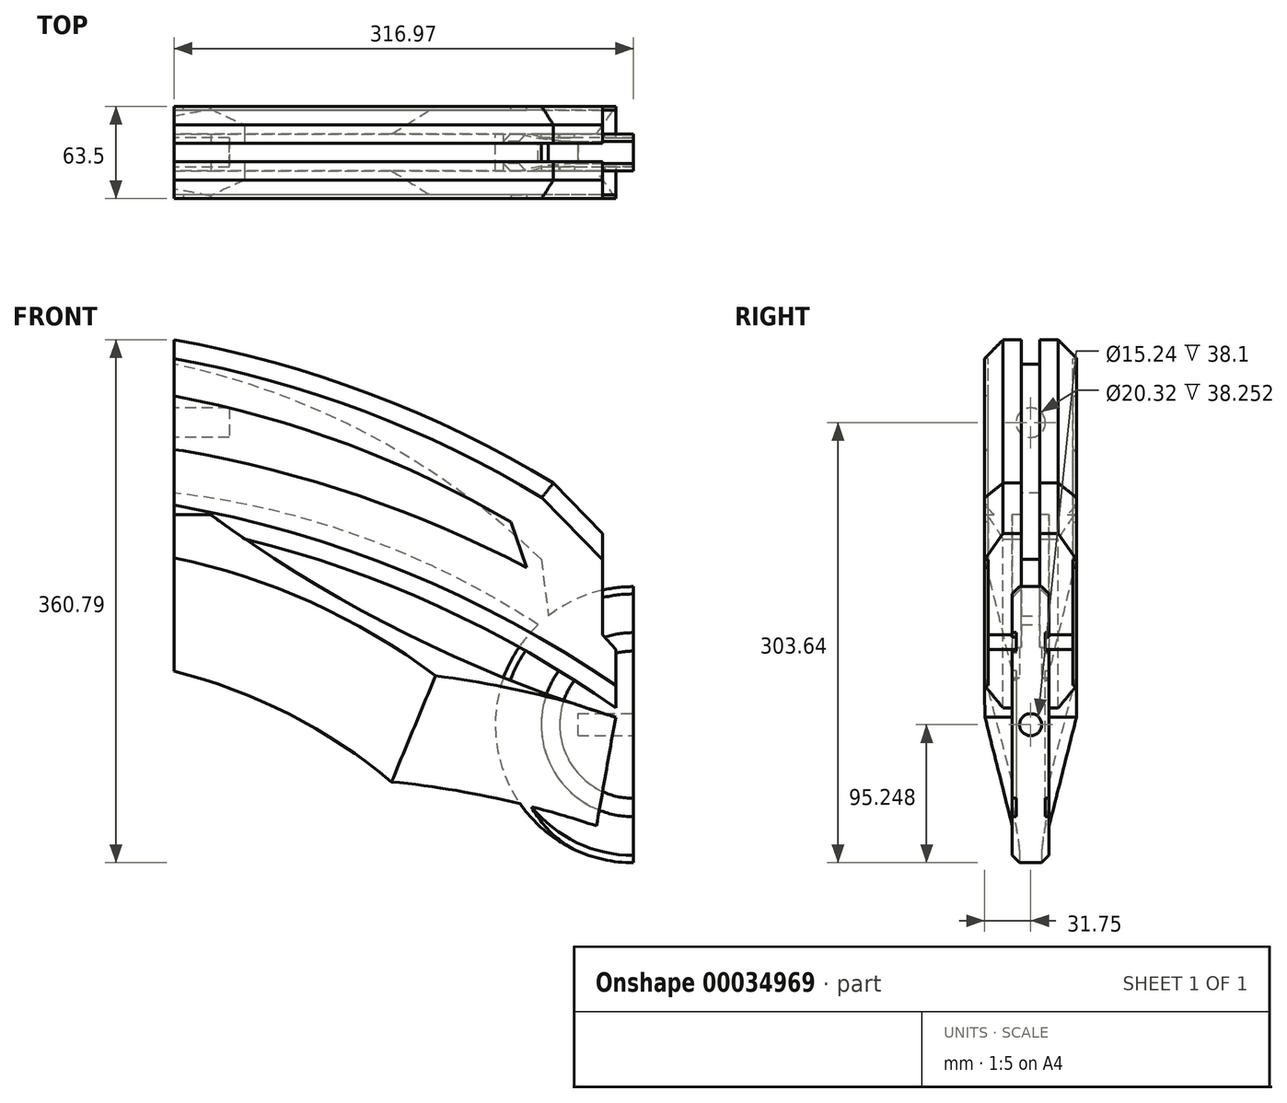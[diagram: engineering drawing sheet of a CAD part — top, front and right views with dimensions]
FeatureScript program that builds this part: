
annotation { "Feature Type Name" : "Feature", "Feature Type Description" : "" }
export const myFeature = defineFeature(function(context is Context, id is Id, definition is map)
    precondition{}
    {
        {
            var Q0;
            Q0=qCreatedBy(makeId("Right.planeOp"),FACE);
            var sketch = newSketch(context, id + "F0", { "sketchPlane" : qUnion([Q0])});
            skCircle(sketch, "E0", {"center": v(0, 0) * mm, "radius": 9.53 * mm});
            skSolve(sketch);
        }
        {
            var Q0;
            Q0=makeQuery(id+"F0.imprint","IMPRINT",FACE,{"disambiguationData":[TD([[makeQuery(id+"F0.imprint","IMPRINT",EDGE,{"derivedFrom":sQuery(id+"F0.wireOp",EDGE,"E0")}),1.0]])]});
            extrude(context, id + "F1", {"entities" : qUnion([Q0]), "depth" : 38.1 * mm});
        }
        {
            var Q0;
            Q0=qCreatedBy(makeId("Front.planeOp"),FACE);
            var sketch = newSketch(context, id + "F2", { "sketchPlane" : qUnion([Q0])});
            skLineSegment(sketch, "E1", {"start": v(37.95, -69.85) * mm, "end": v(37.95, 57.15) * mm});
            skLineSegment(sketch, "E2", {"start": v(342.75, -156.44) * mm, "end": v(342.75, -196.85) * mm});
            skArc(sketch, "E3", {"start": v(299.75, -41.71) * mm, "mid": v(173.43, 19.84) * mm, "end": v(37.95, 57.15) * mm});
            skArc(sketch, "E4", {"start": v(342.75, -196.85) * mm, "mid": v(197.3, -116.64) * mm, "end": v(37.95, -69.85) * mm});
            skLineSegment(sketch, "E5", {"start": v(342.75, -156.44) * mm, "end": v(333.76, -146.22) * mm});
            skLineSegment(sketch, "E6", {"start": v(333.76, -146.22) * mm, "end": v(333.76, -76.46) * mm});
            skLineSegment(sketch, "E7", {"start": v(333.76, -76.46) * mm, "end": v(299.75, -41.71) * mm});
            skSolve(sketch);
        }
        {
            var Q0;
            Q0=makeQuery(id+"F2.imprint","IMPRINT",FACE,{"disambiguationData":[TD([[makeQuery(id+"F2.imprint","IMPRINT",EDGE,{"derivedFrom":sQuery(id+"F2.wireOp",EDGE,"E1")}),-1.0]])]});
            var Q1;
            Q1=makeQuery(id+"F2.imprint","IMPRINT",FACE,{"disambiguationData":[TD([[makeQuery(id+"F2.imprint","IMPRINT",EDGE,{"derivedFrom":sQuery(id+"F2.wireOp",EDGE,"c96b9fbb-76f4-4b25-880c-d232280712f3")}),-1.0]])]});
            extrude(context, id + "F3", {"entities" : qUnion([Q0, Q1]), "operationType" : NewBodyOperationType.ADD, "endBound" : BoundingType.SYMMETRIC, "depth" : 63.5 * mm});
        }
        {
            var Q0;
            Q0=qCreatedBy(makeId("Front.planeOp"),FACE);
            var sketch = newSketch(context, id + "F4", { "sketchPlane" : qUnion([Q0])});
            skLineSegment(sketch, "E8.0", {"start": v(37.95, -69.85) * mm, "end": v(37.95, -48.49) * mm});
            skArc(sketch, "E8.1", {"start": v(299.75, -41.71) * mm, "mid": v(173.43, 19.84) * mm, "end": v(37.95, 57.15) * mm});
            skLineSegment(sketch, "E8.2", {"start": v(333.76, -76.46) * mm, "end": v(299.75, -41.71) * mm});
            skLineSegment(sketch, "E8.3", {"start": v(333.76, -146.22) * mm, "end": v(333.76, -76.46) * mm});
            skLineSegment(sketch, "E8.4", {"start": v(342.75, -156.44) * mm, "end": v(333.76, -146.22) * mm});
            skLineSegment(sketch, "E8.5", {"start": v(342.75, -156.44) * mm, "end": v(342.75, -196.85) * mm});
            skArc(sketch, "E8.6", {"start": v(342.75, -196.85) * mm, "mid": v(197.3, -116.64) * mm, "end": v(37.95, -69.85) * mm});
            skLineSegment(sketch, "E9.trimOffspring", {"start": v(37.95, 40.42) * mm, "end": v(37.95, 57.15) * mm});
            skArc(sketch, "E10", {"start": v(297.91, -145.2) * mm, "mid": v(173.78, -81.12) * mm, "end": v(37.95, -48.49) * mm});
            skArc(sketch, "E11", {"start": v(291.38, -94.3) * mm, "mid": v(174.1, -9.17) * mm, "end": v(37.95, 40.42) * mm});
            skLineSegment(sketch, "E12", {"start": v(291.38, -94.3) * mm, "end": v(297.91, -145.2) * mm});
            skSolve(sketch);
        }
        {
            var Q0;
            Q0=qSketchRegion(id+"F4",true);
            extrude(context, id + "F5", {"entities" : qUnion([Q0]), "operationType" : NewBodyOperationType.REMOVE, "endBound" : BoundingType.SYMMETRIC, "oppositeDirection" : true, "depth" : 12.7 * mm});
        }
        {
            var Q0;
            Q0=makeQuery(id+"F3.opExtrude","CAP_EDGE",EDGE,{"disambiguationData":[OSD([sQuery(id+"F2.wireOp",EDGE,"E3")])],"isStart":false});
            var Q1;
            Q1=makeQuery(id+"F3.opExtrude","CAP_EDGE",EDGE,{"disambiguationData":[OSD([sQuery(id+"F2.wireOp",EDGE,"E7")])],"isStart":false});
            var Q2;
            Q2=makeQuery(id+"F3.opExtrude","CAP_EDGE",EDGE,{"disambiguationData":[OSD([sQuery(id+"F2.wireOp",EDGE,"E7")])],"isStart":true});
            var Q3;
            Q3=makeQuery(id+"F3.opExtrude","CAP_EDGE",EDGE,{"disambiguationData":[OSD([sQuery(id+"F2.wireOp",EDGE,"E3")])],"isStart":true});
            chamfer(context, id + "F6", {"entities" : qUnion([Q0, Q1, Q2, Q3]), "width" : 12.7 * mm, "tangentPropagation" : true});
        }
        {
            var Q0;
            Q0=makeQuery(id+"F3.opExtrude","CAP_EDGE",EDGE,{"disambiguationData":[OSD([sQuery(id+"F2.wireOp",EDGE,"E4")])],"isStart":false});
            var Q1;
            Q1=makeQuery(id+"F3.opExtrude","CAP_EDGE",EDGE,{"disambiguationData":[OSD([sQuery(id+"F2.wireOp",EDGE,"E4")])],"isStart":true});
            chamfer(context, id + "F7", {"entities" : qUnion([Q0, Q1]), "width" : 12.7 * mm, "tangentPropagation" : true});
        }
        {
            var Q0;
            Q0=qCreatedBy(makeId("Front.planeOp"),FACE);
            var sketch = newSketch(context, id + "F8", { "sketchPlane" : qUnion([Q0])});
            skLineSegment(sketch, "E13.0", {"start": v(37.95, -56.95) * mm, "end": v(37.95, 44.25) * mm});
            skFitSpline(sketch, "E13.1", {"points": [v(37.95, -69.85) * mm, v(37.95, -65.55) * mm, v(37.95, -61.25) * mm, v(37.95, -56.95) * mm]});
            skLineSegment(sketch, "E14", {"start": v(37.95, -69.85) * mm, "end": v(37.95, -171.45) * mm});
            skArc(sketch, "E15.0", {"start": v(342.75, -196.85) * mm, "mid": v(197.3, -116.64) * mm, "end": v(37.95, -69.85) * mm});
            skLineSegment(sketch, "E16", {"start": v(37.95, -63.56) * mm, "end": v(63.35, -63.56) * mm});
            skArc(sketch, "E17", {"start": v(63.35, -63.56) * mm, "mid": v(197.17, -145.14) * mm, "end": v(342.75, -203.2) * mm});
            skLineSegment(sketch, "E18", {"start": v(342.75, -203.2) * mm, "end": v(329.52, -278.24) * mm});
            skArc(sketch, "E19", {"start": v(188.13, -247.8) * mm, "mid": v(117.37, -201.1) * mm, "end": v(37.95, -171.45) * mm});
            skArc(sketch, "E20", {"start": v(329.52, -278.24) * mm, "mid": v(259.68, -259.03) * mm, "end": v(188.13, -247.8) * mm});
            skSolve(sketch);
        }
        {
            var Q0;
            Q0=qSketchRegion(id+"F8",true);
            extrude(context, id + "F9", {"entities" : qUnion([Q0]), "operationType" : NewBodyOperationType.ADD, "endBound" : BoundingType.SYMMETRIC, "depth" : 63.5 * mm});
        }
        {
            var Q0;
            Q0=qCreatedBy(makeId("Front.planeOp"),FACE);
            var sketch = newSketch(context, id + "F10", { "sketchPlane" : qUnion([Q0])});
            skLineSegment(sketch, "E21.0", {"start": v(37.95, -69.85) * mm, "end": v(37.95, -171.45) * mm});
            skArc(sketch, "E21.1", {"start": v(188.13, -247.8) * mm, "mid": v(117.37, -201.1) * mm, "end": v(37.95, -171.45) * mm});
            skArc(sketch, "E21.2", {"start": v(329.52, -278.24) * mm, "mid": v(259.68, -259.03) * mm, "end": v(188.13, -247.8) * mm});
            skLineSegment(sketch, "E21.3", {"start": v(342.75, -203.2) * mm, "end": v(329.52, -278.24) * mm});
            skArc(sketch, "E21.4", {"start": v(63.35, -63.56) * mm, "mid": v(197.17, -145.14) * mm, "end": v(342.75, -203.2) * mm});
            skLineSegment(sketch, "E21.5", {"start": v(37.95, -63.56) * mm, "end": v(63.35, -63.56) * mm});
            skFitSpline(sketch, "E21.6", {"points": [v(37.95, -69.85) * mm, v(37.95, -65.55) * mm, v(37.95, -61.25) * mm, v(37.95, -56.95) * mm]});
            skSolve(sketch);
        }
        {
            var Q0;
            Q0=qSketchRegion(id+"F10",true);
            extrude(context, id + "F11", {"entities" : qUnion([Q0]), "operationType" : NewBodyOperationType.REMOVE, "endBound" : BoundingType.SYMMETRIC, "oppositeDirection" : true, "depth" : 25.4 * mm});
        }
        {
            var Q0;
            Q0=makeQuery(id+"F9.opExtrude","CAP_EDGE",EDGE,{"disambiguationData":[OSD([sQuery(id+"F8.wireOp",EDGE,"E19")])],"isStart":false});
            var Q1;
            Q1=makeQuery(id+"F9.opExtrude","CAP_EDGE",EDGE,{"disambiguationData":[OSD([sQuery(id+"F8.wireOp",EDGE,"E20")])],"isStart":false});
            chamfer(context, id + "F12", {"entities" : qUnion([Q0, Q1]), "chamferType" : ChamferType.TWO_OFFSETS, "width1" : 19.05 * mm, "oppositeDirection" : false, "width2" : 76.2 * mm, "tangentPropagation" : true});
        }
        {
            var Q0;
            Q0=makeQuery(id+"F9.opExtrude","CAP_EDGE",EDGE,{"disambiguationData":[OSD([sQuery(id+"F8.wireOp",EDGE,"E20")])],"isStart":true});
            var Q1;
            Q1=makeQuery(id+"F9.opExtrude","CAP_EDGE",EDGE,{"disambiguationData":[OSD([sQuery(id+"F8.wireOp",EDGE,"E19")])],"isStart":true});
            chamfer(context, id + "F13", {"entities" : qUnion([Q0, Q1]), "chamferType" : ChamferType.TWO_OFFSETS, "width1" : 76.2 * mm, "oppositeDirection" : false, "width2" : 19.05 * mm, "tangentPropagation" : true});
        }
        {
            var Q0;
            Q0=qCreatedBy(makeId("Front.planeOp"),FACE);
            var sketch = newSketch(context, id + "F14", { "sketchPlane" : qUnion([Q0])});
            skArc(sketch, "E22", {"start": v(354.92, -113.14) * mm, "mid": v(259.67, -208.4) * mm, "end": v(354.92, -303.64) * mm});
            skFitSpline(sketch, "E23.0", {"points": [v(342.75, -203.2) * mm, v(338.34, -228.21) * mm, v(333.93, -253.23) * mm, v(329.52, -278.24) * mm]});
            skLineSegment(sketch, "E24", {"start": v(354.92, -208.4) * mm, "end": v(354.92, -303.64) * mm});
            skLineSegment(sketch, "E25", {"start": v(354.92, -303.64) * mm, "end": v(354.92, -113.14) * mm});
            skSolve(sketch);
        }
        {
            var Q0;
            Q0=makeQuery(id+"F14.imprint","IMPRINT",FACE,{"disambiguationData":[TD([[makeQuery(id+"F14.imprint","IMPRINT",EDGE,{"derivedFrom":sQuery(id+"F14.wireOp",EDGE,"E22")}),1.0]])]});
            extrude(context, id + "F15", {"entities" : qUnion([Q0]), "operationType" : NewBodyOperationType.ADD, "endBound" : BoundingType.SYMMETRIC, "depth" : 25.4 * mm});
        }
        {
            var Q0;
            {var subQ0=sQuery(id+"F14.wireOp",EDGE,"E22");var subQ1=sQuery(id+"F14.wireOp",EDGE,"E25");Q0=makeQuery(id+"F15.boolean.opBoolean","SPLIT",EDGE,{"disambiguationData":[TD([makeQuery(id+"F11.boolean.opBoolean","COPY",FACE,{"derivedFrom":makeQuery(id+"F11.opExtrude","CAP_FACE",FACE,{"disambiguationData":[OSD([sQuery(id+"F10.wireOp",EDGE,"E21.0"),sQuery(id+"F10.wireOp",EDGE,"E21.1"),sQuery(id+"F10.wireOp",EDGE,"E21.2"),sQuery(id+"F10.wireOp",EDGE,"E21.3"),sQuery(id+"F10.wireOp",EDGE,"E21.4"),sQuery(id+"F10.wireOp",EDGE,"E21.5"),sQuery(id+"F10.wireOp",EDGE,"E21.6")])],"isStart":true})}),makeQuery(id+"F12.opChamfer","BLEND_FACE",FACE,{"disambiguationData":[OSD([sQuery(id+"F8.wireOp",EDGE,"E20")])]}),makeQuery(id+"F15.opExtrude","SWEPT_FACE",FACE,{"disambiguationData":[OSD([subQ0])]}),makeQuery(id+"F15.opExtrude","CAP_FACE",FACE,{"disambiguationData":[OSD([subQ0,subQ1])],"isStart":false}),makeQuery(id+"F15.opExtrude","SWEPT_FACE",FACE,{"disambiguationData":[OSD([subQ1])]})])],"derivedFrom":makeQuery(id+"F15.opExtrude","CAP_EDGE",EDGE,{"disambiguationData":[OSD([subQ0])],"isStart":false})});}
            var Q1;
            {var subQ0=sQuery(id+"F14.wireOp",EDGE,"E22");Q1=makeQuery(id+"F15.boolean.opBoolean","SPLIT",EDGE,{"disambiguationData":[TD([makeQuery(id+"F3.opExtrude","SWEPT_FACE",FACE,{"disambiguationData":[OSD([sQuery(id+"F2.wireOp",EDGE,"E4")])]}),makeQuery(id+"F9.opExtrude","SWEPT_FACE",FACE,{"disambiguationData":[OSD([sQuery(id+"F8.wireOp",EDGE,"E17")])]}),makeQuery(id+"F11.boolean.opBoolean","COPY",FACE,{"derivedFrom":makeQuery(id+"F11.opExtrude","CAP_FACE",FACE,{"disambiguationData":[OSD([sQuery(id+"F10.wireOp",EDGE,"E21.0"),sQuery(id+"F10.wireOp",EDGE,"E21.1"),sQuery(id+"F10.wireOp",EDGE,"E21.2"),sQuery(id+"F10.wireOp",EDGE,"E21.3"),sQuery(id+"F10.wireOp",EDGE,"E21.4"),sQuery(id+"F10.wireOp",EDGE,"E21.5"),sQuery(id+"F10.wireOp",EDGE,"E21.6")])],"isStart":true})}),makeQuery(id+"F15.opExtrude","SWEPT_FACE",FACE,{"disambiguationData":[OSD([subQ0])]}),makeQuery(id+"F15.opExtrude","CAP_FACE",FACE,{"disambiguationData":[OSD([subQ0,sQuery(id+"F14.wireOp",EDGE,"E25")])],"isStart":false})])],"derivedFrom":makeQuery(id+"F15.opExtrude","CAP_EDGE",EDGE,{"disambiguationData":[OSD([subQ0])],"isStart":false})});}
            var Q2;
            {var subQ0=sQuery(id+"F14.wireOp",EDGE,"E22");var subQ1=sQuery(id+"F14.wireOp",EDGE,"E25");Q2=makeQuery(id+"F15.boolean.opBoolean","SPLIT",EDGE,{"disambiguationData":[TD([makeQuery(id+"F3.opExtrude","SWEPT_FACE",FACE,{"disambiguationData":[OSD([sQuery(id+"F2.wireOp",EDGE,"E6")])]}),makeQuery(id+"F15.opExtrude","SWEPT_FACE",FACE,{"disambiguationData":[OSD([subQ0])]}),makeQuery(id+"F15.opExtrude","CAP_FACE",FACE,{"disambiguationData":[OSD([subQ0,subQ1])],"isStart":false}),makeQuery(id+"F15.opExtrude","SWEPT_FACE",FACE,{"disambiguationData":[OSD([subQ1])]})])],"derivedFrom":makeQuery(id+"F15.opExtrude","CAP_EDGE",EDGE,{"disambiguationData":[OSD([subQ0])],"isStart":false})});}
            var Q3;
            {var subQ0=sQuery(id+"F14.wireOp",EDGE,"E22");var subQ1=sQuery(id+"F14.wireOp",EDGE,"E25");Q3=makeQuery(id+"F15.boolean.opBoolean","SPLIT",EDGE,{"disambiguationData":[TD([makeQuery(id+"F3.opExtrude","SWEPT_FACE",FACE,{"disambiguationData":[OSD([sQuery(id+"F2.wireOp",EDGE,"E6")])]}),makeQuery(id+"F15.opExtrude","SWEPT_FACE",FACE,{"disambiguationData":[OSD([subQ0])]}),makeQuery(id+"F15.opExtrude","CAP_FACE",FACE,{"disambiguationData":[OSD([subQ0,subQ1])],"isStart":true}),makeQuery(id+"F15.opExtrude","SWEPT_FACE",FACE,{"disambiguationData":[OSD([subQ1])]})])],"derivedFrom":makeQuery(id+"F15.opExtrude","CAP_EDGE",EDGE,{"disambiguationData":[OSD([subQ0])],"isStart":true})});}
            var Q4;
            {var subQ0=sQuery(id+"F14.wireOp",EDGE,"E22");Q4=makeQuery(id+"F15.boolean.opBoolean","SPLIT",EDGE,{"disambiguationData":[TD([makeQuery(id+"F3.opExtrude","SWEPT_FACE",FACE,{"disambiguationData":[OSD([sQuery(id+"F2.wireOp",EDGE,"E4")])]}),makeQuery(id+"F9.opExtrude","SWEPT_FACE",FACE,{"disambiguationData":[OSD([sQuery(id+"F8.wireOp",EDGE,"E17")])]}),makeQuery(id+"F11.boolean.opBoolean","COPY",FACE,{"derivedFrom":makeQuery(id+"F11.opExtrude","CAP_FACE",FACE,{"disambiguationData":[OSD([sQuery(id+"F10.wireOp",EDGE,"E21.0"),sQuery(id+"F10.wireOp",EDGE,"E21.1"),sQuery(id+"F10.wireOp",EDGE,"E21.2"),sQuery(id+"F10.wireOp",EDGE,"E21.3"),sQuery(id+"F10.wireOp",EDGE,"E21.4"),sQuery(id+"F10.wireOp",EDGE,"E21.5"),sQuery(id+"F10.wireOp",EDGE,"E21.6")])],"isStart":false})}),makeQuery(id+"F15.opExtrude","SWEPT_FACE",FACE,{"disambiguationData":[OSD([subQ0])]}),makeQuery(id+"F15.opExtrude","CAP_FACE",FACE,{"disambiguationData":[OSD([subQ0,sQuery(id+"F14.wireOp",EDGE,"E25")])],"isStart":true})])],"derivedFrom":makeQuery(id+"F15.opExtrude","CAP_EDGE",EDGE,{"disambiguationData":[OSD([subQ0])],"isStart":true})});}
            var Q5;
            {var subQ0=sQuery(id+"F14.wireOp",EDGE,"E22");var subQ1=sQuery(id+"F14.wireOp",EDGE,"E25");Q5=makeQuery(id+"F15.boolean.opBoolean","SPLIT",EDGE,{"disambiguationData":[TD([makeQuery(id+"F11.boolean.opBoolean","COPY",FACE,{"derivedFrom":makeQuery(id+"F11.opExtrude","CAP_FACE",FACE,{"disambiguationData":[OSD([sQuery(id+"F10.wireOp",EDGE,"E21.0"),sQuery(id+"F10.wireOp",EDGE,"E21.1"),sQuery(id+"F10.wireOp",EDGE,"E21.2"),sQuery(id+"F10.wireOp",EDGE,"E21.3"),sQuery(id+"F10.wireOp",EDGE,"E21.4"),sQuery(id+"F10.wireOp",EDGE,"E21.5"),sQuery(id+"F10.wireOp",EDGE,"E21.6")])],"isStart":false})}),makeQuery(id+"F13.opChamfer","BLEND_FACE",FACE,{"disambiguationData":[OSD([sQuery(id+"F8.wireOp",EDGE,"E20")])]}),makeQuery(id+"F15.opExtrude","SWEPT_FACE",FACE,{"disambiguationData":[OSD([subQ0])]}),makeQuery(id+"F15.opExtrude","CAP_FACE",FACE,{"disambiguationData":[OSD([subQ0,subQ1])],"isStart":true}),makeQuery(id+"F15.opExtrude","SWEPT_FACE",FACE,{"disambiguationData":[OSD([subQ1])]})])],"derivedFrom":makeQuery(id+"F15.opExtrude","CAP_EDGE",EDGE,{"disambiguationData":[OSD([subQ0])],"isStart":true})});}
            chamfer(context, id + "F16", {"entities" : qUnion([Q0, Q1, Q2, Q3, Q4, Q5]), "width" : 5.08 * mm, "tangentPropagation" : true});
        }
        {
            var Q0;
            Q0=makeQuery(id+"F3.opExtrude","CAP_FACE",FACE,{"disambiguationData":[OSD([sQuery(id+"F2.wireOp",EDGE,"E1"),sQuery(id+"F2.wireOp",EDGE,"E2"),sQuery(id+"F2.wireOp",EDGE,"E3"),sQuery(id+"F2.wireOp",EDGE,"E4"),sQuery(id+"F2.wireOp",EDGE,"E5"),sQuery(id+"F2.wireOp",EDGE,"E6"),sQuery(id+"F2.wireOp",EDGE,"E7")])],"isStart":false});
            var sketch = newSketch(context, id + "F17", { "sketchPlane" : qUnion([Q0])});
            skArc(sketch, "E26.0", {"start": v(37.95, -56.95) * mm, "mid": v(197.03, -102.8) * mm, "end": v(342.75, -181.38) * mm});
            skArc(sketch, "E26.1", {"start": v(291.8, -51.75) * mm, "mid": v(169.26, 7.84) * mm, "end": v(37.95, 44.25) * mm});
            skLineSegment(sketch, "E26.2", {"start": v(37.95, -56.95) * mm, "end": v(37.95, 44.25) * mm});
            skArc(sketch, "E27.0", {"start": v(44.52, -19.43) * mm, "mid": v(166.02, -50.54) * mm, "end": v(281.28, -99.97) * mm});
            skArc(sketch, "E28.0", {"start": v(270.5, -68.62) * mm, "mid": v(157.98, -15.06) * mm, "end": v(37.95, 18.42) * mm});
            skLineSegment(sketch, "E29", {"start": v(44.52, -19.43) * mm, "end": v(37.95, -18.78) * mm});
            skLineSegment(sketch, "E30", {"start": v(270.5, -68.62) * mm, "end": v(281.28, -99.97) * mm});
            skSolve(sketch);
        }
        {
            var Q0;
            Q0=makeQuery(id+"F17.imprint","IMPRINT",FACE,{"disambiguationData":[TD([[makeQuery(id+"F17.imprint","IMPRINT",EDGE,{"derivedFrom":sQuery(id+"F17.wireOp",EDGE,"E27.0")}),1.0]])]});
            extrude(context, id + "F18", {"entities" : qUnion([Q0]), "operationType" : NewBodyOperationType.REMOVE, "oppositeDirection" : true, "depth" : 2.54 * mm});
        }
        {
            var Q0;
            Q0=makeQuery(id+"F3.opExtrude","CAP_FACE",FACE,{"disambiguationData":[OSD([sQuery(id+"F2.wireOp",EDGE,"E1"),sQuery(id+"F2.wireOp",EDGE,"E2"),sQuery(id+"F2.wireOp",EDGE,"E3"),sQuery(id+"F2.wireOp",EDGE,"E4"),sQuery(id+"F2.wireOp",EDGE,"E5"),sQuery(id+"F2.wireOp",EDGE,"E6"),sQuery(id+"F2.wireOp",EDGE,"E7")])],"isStart":true});
            var sketch = newSketch(context, id + "F19", { "sketchPlane" : qUnion([Q0])});
            skArc(sketch, "E31.0", {"start": v(-270.5, -68.62) * mm, "mid": v(-157.98, -15.06) * mm, "end": v(-37.95, 18.42) * mm});
            skArc(sketch, "E31.1", {"start": v(-44.52, -19.43) * mm, "mid": v(-166.02, -50.54) * mm, "end": v(-281.28, -99.97) * mm});
            skLineSegment(sketch, "E31.2", {"start": v(-44.52, -19.43) * mm, "end": v(-37.95, -18.78) * mm});
            skLineSegment(sketch, "E31.3", {"start": v(-270.5, -68.62) * mm, "end": v(-281.28, -99.97) * mm});
            skSolve(sketch);
        }
        {
            var Q0;
            {var subQ2=sQuery(id+"F19.wireOp",EDGE,"E31.0");Q0=makeQuery(id+"F19.imprint","IMPRINT",FACE,{"disambiguationData":[TD([[makeQuery(id+"F19.imprint","IMPRINT",EDGE,{"derivedFrom":subQ2}),-1.0]])]});}
            extrude(context, id + "F20", {"entities" : qUnion([Q0]), "operationType" : NewBodyOperationType.REMOVE, "oppositeDirection" : true, "depth" : 2.54 * mm});
        }
        {
            var Q0;
            Q0=makeQuery(id+"F15.opExtrude","SWEPT_FACE",FACE,{"disambiguationData":[OSD([sQuery(id+"F14.wireOp",EDGE,"E25")])]});
            var sketch = newSketch(context, id + "F21", { "sketchPlane" : qUnion([Q0])});
            skLineSegment(sketch, "E32", {"start": v(0, -303.64) * mm, "end": v(0, -113.14) * mm, "construction": true});
            skCircle(sketch, "E33", {"center": v(0, -208.4) * mm, "radius": 7.62 * mm});
            skSolve(sketch);
        }
        {
            var Q0;
            Q0=makeQuery(id+"F21.imprint","IMPRINT",FACE,{"disambiguationData":[TD([[makeQuery(id+"F21.imprint","IMPRINT",EDGE,{"derivedFrom":sQuery(id+"F21.wireOp",EDGE,"E33")}),1.0]])]});
            extrude(context, id + "F22", {"entities" : qUnion([Q0]), "operationType" : NewBodyOperationType.REMOVE, "oppositeDirection" : true, "depth" : 38.1 * mm});
        }
        {
            var Q0;
            Q0=makeQuery(id+"F15.opExtrude","CAP_FACE",FACE,{"disambiguationData":[OSD([sQuery(id+"F14.wireOp",EDGE,"E22"),sQuery(id+"F14.wireOp",EDGE,"E25")])],"isStart":false});
            var sketch = newSketch(context, id + "F23", { "sketchPlane" : qUnion([Q0])});
            skLineSegment(sketch, "E34.0", {"start": v(354.92, -298.56) * mm, "end": v(354.92, -118.22) * mm});
            skCircle(sketch, "E35", {"center": v(354.92, -208.4) * mm, "radius": 50.8 * mm});
            skCircle(sketch, "E36", {"center": v(354.92, -208.4) * mm, "radius": 63.5 * mm});
            skSolve(sketch);
        }
        {
            var Q0;
            {var subQ14=sQuery(id+"F23.wireOp",EDGE,"E36");var subQ16=sQuery(id+"F23.wireOp",EDGE,"E34.0");var subQ17=makeQuery(id+"F23.imprint","INTERSECT",VERTEX,{"disambiguationData":[OD(1.0)],"derivedFrom":[subQ16,subQ14]});Q0=makeQuery(id+"F23.imprint","IMPRINT",FACE,{"disambiguationData":[TD([[makeQuery(id+"F23.imprint","IMPRINT",EDGE,{"disambiguationData":[TD([[subQ17,1.0]])],"derivedFrom":subQ16}),1.0]])]});}
            var Q1;
            {var subQ6=sQuery(id+"F23.wireOp",EDGE,"E35");var subQ10=sQuery(id+"F10.wireOp",EDGE,"E21.4");var subQ11=makeQuery(id+"F15.boolean.opBoolean","SPLIT",EDGE,{"disambiguationData":[TD([makeQuery(id+"F9.opExtrude","SWEPT_FACE",FACE,{"disambiguationData":[OSD([sQuery(id+"F8.wireOp",EDGE,"E18")])]})])],"derivedFrom":makeQuery(id+"F11.boolean.opBoolean","COPY",EDGE,{"disambiguationData":[OD(0.0)],"derivedFrom":makeQuery(id+"F11.opExtrude","CAP_EDGE",EDGE,{"disambiguationData":[OSD([subQ10])],"isStart":true})})});var subQ12=makeQuery(id+"F23.imprint","INTERSECT",VERTEX,{"derivedFrom":[subQ11,subQ6]});Q1=makeQuery(id+"F23.imprint","IMPRINT",FACE,{"disambiguationData":[TD([[makeQuery(id+"F23.imprint","IMPRINT",EDGE,{"disambiguationData":[TD([[subQ12,1.0]])],"derivedFrom":subQ6}),-1.0]])]});}
            var Q2;
            {var subQ3=sQuery(id+"F23.wireOp",EDGE,"E36");var subQ5=sQuery(id+"F23.wireOp",EDGE,"E34.0");var subQ6=makeQuery(id+"F23.imprint","INTERSECT",VERTEX,{"disambiguationData":[OD(0.0)],"derivedFrom":[subQ5,subQ3]});Q2=makeQuery(id+"F23.imprint","IMPRINT",FACE,{"disambiguationData":[TD([[makeQuery(id+"F23.imprint","IMPRINT",EDGE,{"disambiguationData":[TD([[subQ6,-1.0]])],"derivedFrom":subQ5}),1.0]])]});}
            extrude(context, id + "F24", {"entities" : qUnion([Q0, Q1, Q2]), "operationType" : NewBodyOperationType.REMOVE, "oppositeDirection" : true, "depth" : 2.8 * mm});
        }
        {
            var Q0;
            Q0=makeQuery(id+"F15.opExtrude","CAP_FACE",FACE,{"disambiguationData":[OSD([sQuery(id+"F14.wireOp",EDGE,"E22"),sQuery(id+"F14.wireOp",EDGE,"E25")])],"isStart":true});
            var sketch = newSketch(context, id + "F25", { "sketchPlane" : qUnion([Q0])});
            skLineSegment(sketch, "E37.0", {"start": v(-354.92, -298.56) * mm, "end": v(-354.92, -118.22) * mm});
            skCircle(sketch, "E38", {"center": v(-354.92, -208.4) * mm, "radius": 50.8 * mm});
            skCircle(sketch, "E39", {"center": v(-354.92, -208.4) * mm, "radius": 63.5 * mm});
            skSolve(sketch);
        }
        {
            var Q0;
            {var subQ14=sQuery(id+"F25.wireOp",EDGE,"E39");var subQ16=sQuery(id+"F25.wireOp",EDGE,"E37.0");var subQ17=makeQuery(id+"F25.imprint","INTERSECT",VERTEX,{"disambiguationData":[OD(1.0)],"derivedFrom":[subQ16,subQ14]});Q0=makeQuery(id+"F25.imprint","IMPRINT",FACE,{"disambiguationData":[TD([[makeQuery(id+"F25.imprint","IMPRINT",EDGE,{"disambiguationData":[TD([[subQ17,1.0]])],"derivedFrom":subQ16}),-1.0]])]});}
            var Q1;
            {var subQ6=sQuery(id+"F25.wireOp",EDGE,"E38");var subQ10=sQuery(id+"F10.wireOp",EDGE,"E21.4");var subQ11=makeQuery(id+"F15.boolean.opBoolean","SPLIT",EDGE,{"disambiguationData":[TD([makeQuery(id+"F9.opExtrude","SWEPT_FACE",FACE,{"disambiguationData":[OSD([sQuery(id+"F8.wireOp",EDGE,"E18")])]})])],"derivedFrom":makeQuery(id+"F11.boolean.opBoolean","COPY",EDGE,{"disambiguationData":[OD(0.0)],"derivedFrom":makeQuery(id+"F11.opExtrude","CAP_EDGE",EDGE,{"disambiguationData":[OSD([subQ10])],"isStart":false})})});var subQ12=makeQuery(id+"F25.imprint","INTERSECT",VERTEX,{"derivedFrom":[subQ11,subQ6]});Q1=makeQuery(id+"F25.imprint","IMPRINT",FACE,{"disambiguationData":[TD([[makeQuery(id+"F25.imprint","IMPRINT",EDGE,{"disambiguationData":[TD([[subQ12,-1.0]])],"derivedFrom":subQ6}),-1.0]])]});}
            var Q2;
            {var subQ3=sQuery(id+"F25.wireOp",EDGE,"E39");var subQ5=sQuery(id+"F25.wireOp",EDGE,"E37.0");var subQ7=makeQuery(id+"F25.imprint","INTERSECT",VERTEX,{"disambiguationData":[OD(0.0)],"derivedFrom":[subQ5,subQ3]});Q2=makeQuery(id+"F25.imprint","IMPRINT",FACE,{"disambiguationData":[TD([[makeQuery(id+"F25.imprint","IMPRINT",EDGE,{"disambiguationData":[TD([[subQ7,-1.0]])],"derivedFrom":subQ5}),-1.0]])]});}
            extrude(context, id + "F26", {"entities" : qUnion([Q0, Q1, Q2]), "operationType" : NewBodyOperationType.REMOVE, "oppositeDirection" : true, "depth" : 2.54 * mm});
        }
        {
            var Q0;
            Q0=makeQuery(id+"F1.opExtrude","CAP_FACE",FACE,{"disambiguationData":[OSD([sQuery(id+"F0.wireOp",EDGE,"E0")])],"isStart":true});
            var sketch = newSketch(context, id + "F27", { "sketchPlane" : qUnion([Q0])});
            skCircle(sketch, "E40.0", {"center": v(0, 0) * mm, "radius": 9.53 * mm});
            skCircle(sketch, "E41", {"center": v(0, 0) * mm, "radius": 10.16 * mm});
            skSolve(sketch);
        }
        {
            var Q0;
            Q0=qSketchRegion(id+"F27",true);
            var Q1;
            Q1=makeQuery(id+"F27.imprint","IMPRINT",FACE,{"disambiguationData":[TD([[makeQuery(id+"F27.imprint","IMPRINT",EDGE,{"derivedFrom":sQuery(id+"F27.wireOp",EDGE,"E40.0")}),-1.0]])]});
            extrude(context, id + "F28", {"entities" : qUnion([Q0, Q1]), "operationType" : NewBodyOperationType.REMOVE, "oppositeDirection" : true, "depth" : 76.2 * mm});
        }
    });
